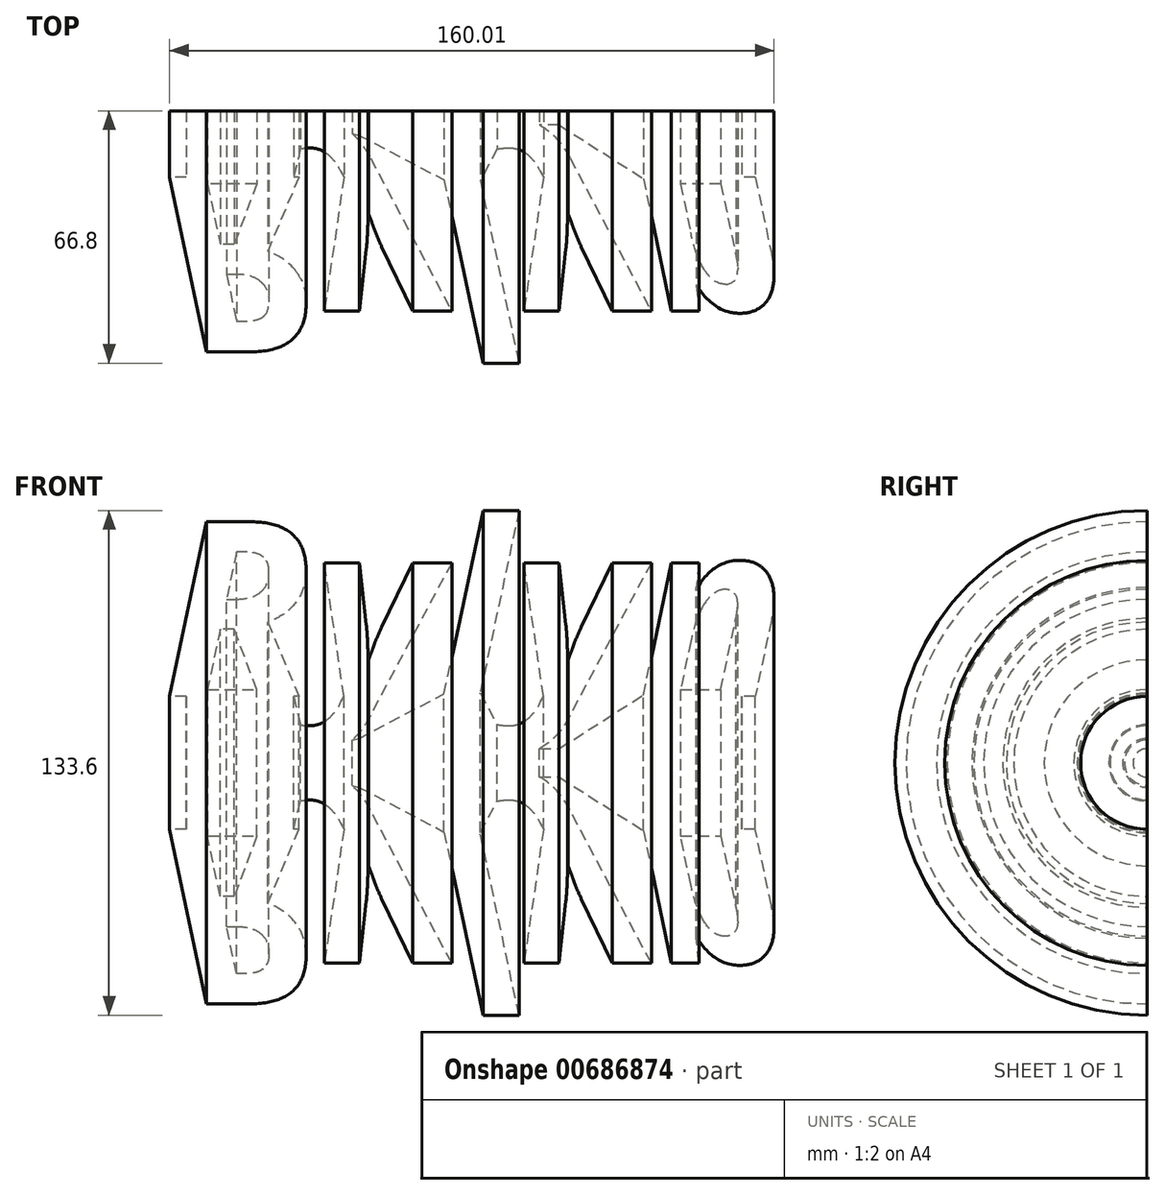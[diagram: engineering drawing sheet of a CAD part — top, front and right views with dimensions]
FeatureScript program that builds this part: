
annotation { "Feature Type Name" : "Feature", "Feature Type Description" : "" }
export const myFeature = defineFeature(function(context is Context, id is Id, definition is map)
    precondition{}
    {
        {
            var Q0;
            Q0=qCreatedBy(makeId("Front.planeOp"),FACE);
            var sketch = newSketch(context, id + "F0", { "sketchPlane" : qUnion([Q0])});
            skText(sketch, "E0", { "text": "Rylyn", "fontName": "OpenSans-BoldItalic.ttf"});
            skLineSegment(sketch, "E1", {"start": v(-76.55, 0) * mm, "end": v(78.66, 0) * mm, "construction": true});
            const initialGuessF0  = {"E0": [-0.07384, 0.0176, 1, 0, 0.04662]};
            skSetInitialGuess(sketch, initialGuessF0);
            skSolve(sketch);
        }
        {
            var Q0;
            Q0 = qSketchRegion(id + "F0", true);
            var Q1;
            Q1=sQuery(id+"F0.wireOp",EDGE,"E1");
            revolve(context, id + "F1", {"entities" : qUnion([Q0]), "axis" : qUnion([Q1]), "revolveType" : RevolveType.ONE_DIRECTION, "angle" : 180 * degree});
        }
        {
            var Q0;
            Q0=qCreatedBy(makeId("Front.planeOp"),FACE);
            var sketch = newSketch(context, id + "F2", { "sketchPlane" : qUnion([Q0])});
            skLineSegment(sketch, "E2", {"start": v(79.37, 0) * mm, "end": v(-67.71, 0) * mm});
            skLineSegment(sketch, "E3", {"start": v(-67.71, 0) * mm, "end": v(-67.71, 19.4) * mm});
            skLineSegment(sketch, "E4", {"start": v(-67.71, 19.4) * mm, "end": v(-39.74, 19.4) * mm});
            skLineSegment(sketch, "E5", {"start": v(-39.74, 19.4) * mm, "end": v(-35.83, 3.16) * mm});
            skLineSegment(sketch, "E6", {"start": v(-35.83, 3.16) * mm, "end": v(-22.08, 6.47) * mm});
            skLineSegment(sketch, "E7", {"start": v(-22.08, 6.47) * mm, "end": v(2.67, 19.4) * mm});
            skLineSegment(sketch, "E8", {"start": v(2.67, 19.4) * mm, "end": v(9.59, 19.4) * mm});
            skLineSegment(sketch, "E9", {"start": v(9.59, 19.4) * mm, "end": v(16.2, 7.07) * mm});
            skLineSegment(sketch, "E10", {"start": v(16.2, 7.07) * mm, "end": v(22.52, 3.76) * mm});
            skLineSegment(sketch, "E11", {"start": v(22.52, 3.76) * mm, "end": v(30.94, 3.76) * mm});
            skLineSegment(sketch, "E12", {"start": v(30.94, 3.76) * mm, "end": v(55.6, 19.4) * mm});
            skLineSegment(sketch, "E13", {"start": v(55.6, 19.4) * mm, "end": v(79.37, 19.4) * mm});
            skLineSegment(sketch, "E14", {"start": v(79.37, 19.4) * mm, "end": v(79.37, 0) * mm});
            skSolve(sketch);
        }
        {
            var Q0;
            Q0 = qSketchRegion(id + "F2", true);
            var Q1;
            Q1=sQuery(id+"F2.wireOp",EDGE,"E2");
            revolve(context, id + "F3", {"operationType" : NewBodyOperationType.ADD, "entities" : qUnion([Q0]), "axis" : qUnion([Q1]), "revolveType" : RevolveType.ONE_DIRECTION, "oppositeDirection" : true, "angle" : 180 * degree});
        }
    });
